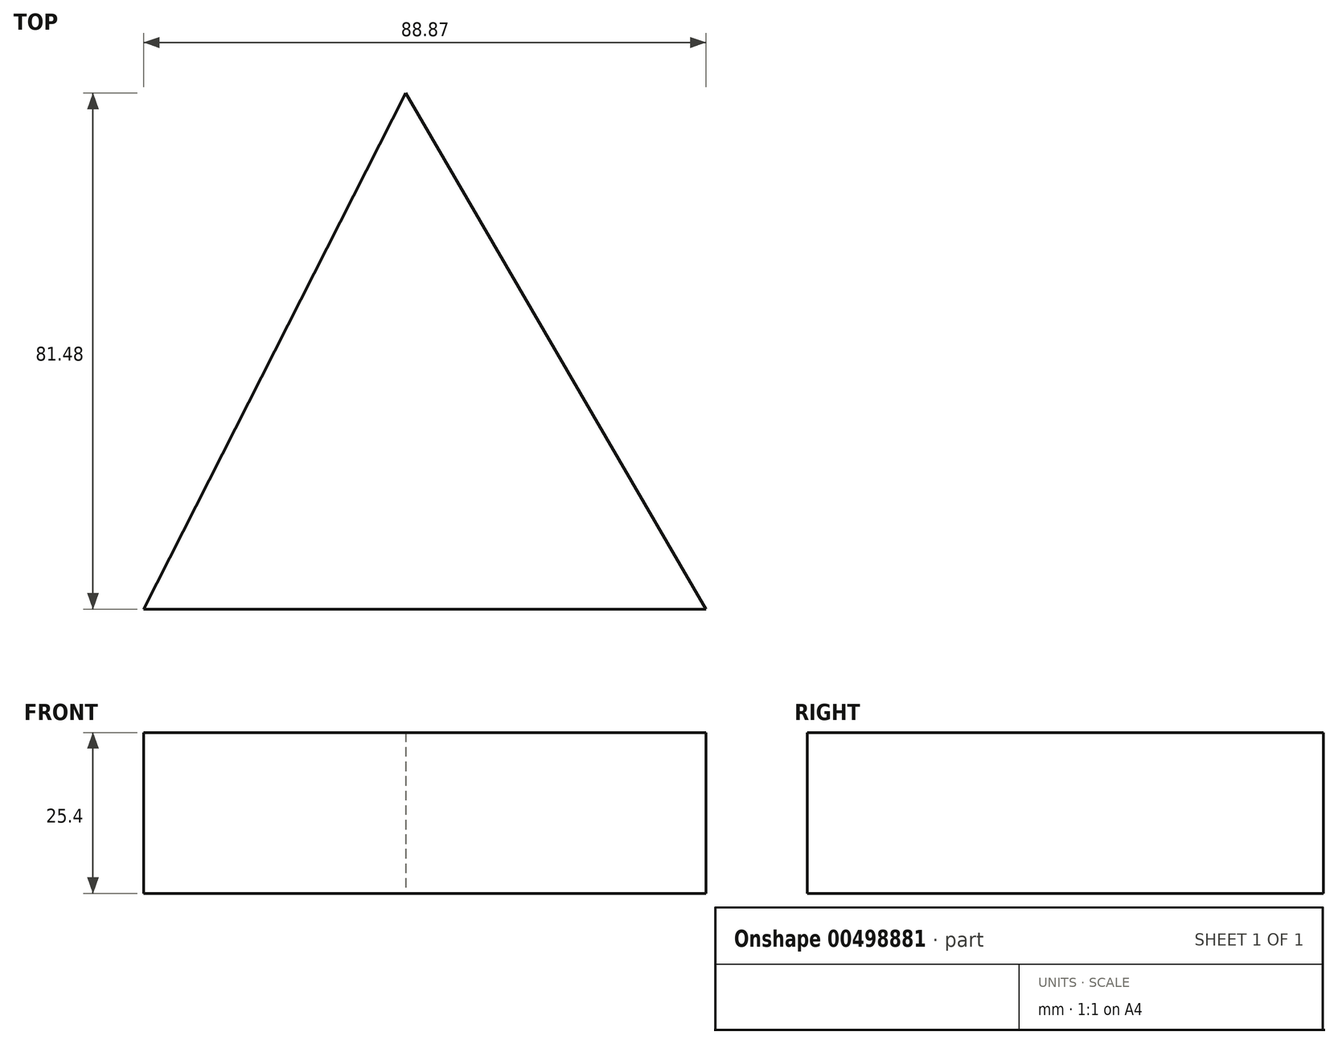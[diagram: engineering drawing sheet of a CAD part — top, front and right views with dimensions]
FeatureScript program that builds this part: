
annotation { "Feature Type Name" : "Feature", "Feature Type Description" : "" }
export const myFeature = defineFeature(function(context is Context, id is Id, definition is map)
    precondition{}
    {
        {
            var Q0;
            Q0=qCreatedBy(makeId("Top.planeOp"),FACE);
            var sketch = newSketch(context, id + "F0", { "sketchPlane" : qUnion([Q0])});
            skLineSegment(sketch, "E0", {"start": v(0, 81.48) * mm, "end": v(47.48, 0) * mm});
            skLineSegment(sketch, "E1", {"start": v(47.48, 0) * mm, "end": v(-41.4, 0) * mm});
            skLineSegment(sketch, "E2", {"start": v(-41.4, 0) * mm, "end": v(0, 81.48) * mm});
            skSolve(sketch);
        }
        {
            var Q0;
            Q0 = qSketchRegion(id + "F0", true);
            var Q1;
            Q1=makeQuery(id+"F0.imprint","IMPRINT",FACE,{"disambiguationData":[TD([[makeQuery(id+"F0.imprint","IMPRINT",EDGE,{"derivedFrom":sQuery(id+"F0.wireOp",EDGE,"E0")}),-1.0]])]});
            extrude(context, id + "F1", {"entities" : qUnion([Q0, Q1]), "depth" : 25.4 * mm});
        }
    });
